SOLIDWORKS PART (.sldprt)
format: sldprt  version: not decoded by parser v0  size: 273,920 bytes
history: native  units: mm
features: sketch x20, extrude x14, plane x9, revolve x2, material x1, shell x1 (+10 scaffold rows collapsed)
feature tree (57):
  scaffold x10  (default folders/planes/origin — collapsed)
  material  "Matériau <non spécifié>"
  plane  "Plan de face"
  plane  "Plan de dessus"
  plane  "Plan de droite"
  sketch  "Esquisse1"  dims[D1=10.0mm D2=20.0mm]
  extrude  "pivot moteur"  Depth=55mm
  plane  "Plan1"  Offset=5mm
  sketch  "Esquisse2"  dims[D1=10.0mm]
  extrude  "Extrusion2"  Depth=50mm
  plane  "Plan2"  Offset=25mm
  sketch  "Esquisse3"  dims[c1.D2=10.0mm c1.D4=20.0mm c1.D3=20.0mm c1.D1=70.0mm c2.D3=23.6mm]
  extrude  "pivot intermediaire"  Depth=55mm
  sketch  "Esquisse4"  dims[D1=10.0mm D2=50.0mm]
  extrude  "Extrusion4"  Depth=70mm
  sketch  "Esquisse5"
  plane  "Plan3"
  sketch  "Esquisse6"  dims[D1=10.0mm]
  extrude  "Extrusion5"  Depth=18.6mm
  sketch  "Esquisse28"  dims[D1=0.0mm]
  sketch  "Esquisse8"
  extrude  "Extrusion6"  Depth=70mm
  plane  "Plan4"  Offset=115mm
  sketch  "Esquisse9"  dims[c1.D2=~43.738123mm c1.D3=10.0mm c1.D4=20.0mm c1.D1=5.5mm c2.D2=130.0mm c2.D1=17.0mm]
  extrude  "pivot sortie"  Depth=55mm
  sketch  "Esquisse11"
  sketch  "Esquisse12"  dims[D1=10.0mm]
  extrude  "Extrusion8"  Depth=17mm
  sketch  "Esquisse14"
  revolve  "Révolution2"  Angle=90deg
  sketch  "Esquisse15"
  plane  "Plan6"
  sketch  "Esquisse17"  dims[D1=10.0mm]
  extrude  "Extrusion9"  Depth=70mm
  sketch  "Esquisse18"
  revolve  "Révolution3"  Angle=90deg
  sketch  "Esquisse21"  dims[D1=10.0mm D2=15.0mm]
  extrude  "Extrusion18"  Depth=115.5mm
  plane  "Plan7"  Offset=30mm
  sketch  "Esquisse29"  dims[c1.D3=20.0mm c1.D1=200.0mm c1.D2=200.0mm c2.D3=67.0mm]
  extrude  "Extrusion19"  Depth=150mm
  shell  "Coque2"  Thickness=4mm
  sketch  "Esquisse19"  dims[c1.D1=10.0mm c1.D2=20.0mm c1.D4=10.0mm c1.D5=20.0mm c2.D4=20.0mm c2.D3=278.51mm c3.D4=97.0mm c3.D5=30.0mm c4.D4=30.0mm c4.D3=20.0mm]
  extrude  "pivot vantail"  Depth=55mm
  sketch  "Esquisse30"  dims[D1=10.0mm D2=27.5mm]
  extrude  "Extrusion21"  [1 undecoded]
  sketch  "Esquisse31"  dims[c1.D1=50.0mm c1.D2=50.0mm c1.D3=50.0mm c1.D4=200.0mm c1.D5=700.0mm c2.D2=250.0mm]
  extrude  "mur"  [1 undecoded]
decode coverage: 29 of 37 modeling features carry decoded parameters
note: ~ marks probable driven/reference dimensions
note: 2 parameter values undecoded
note: suppression state not decoded; provenance and decode notes live in map.json
